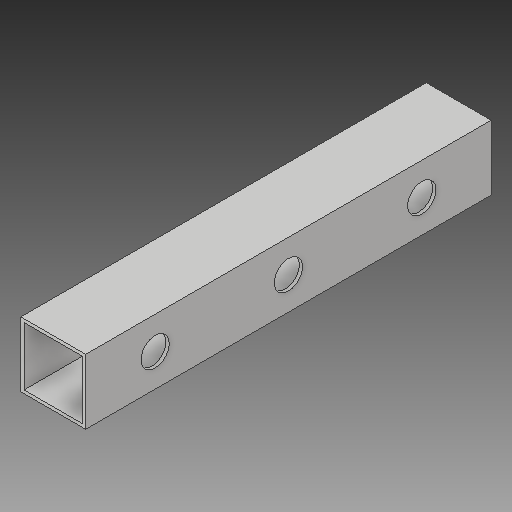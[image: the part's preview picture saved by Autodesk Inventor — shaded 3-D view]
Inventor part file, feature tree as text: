
AUTODESK INVENTOR PART (.ipt)
format: ipt  version: 2018 (Build 220112000, 112)  size: 115,200 bytes
history: native  units: mm
features: other x2, sketch x2, extrude x1, hole x1
ambient origin geometry x8: Origin, YZ Plane, XZ Plane, XY Plane, X Axis, Y Axis, Z Axis, Center Point
bodies: Body1 (feature_tree)
feature tree (6):
  other  "ソリッド1"
  extrude  "押し出し1"  Depth=32.0mm
  other  "作業平面1"
  hole  "穴2"  [1 undecoded]
  sketch  "スケッチ1"
  sketch  "スケッチ6"
note: 1 required parameter value undecoded (feature->parameter linkage not recoverable at this tier; creation-order binding heuristic only, values carry confidence <= 0.55)
